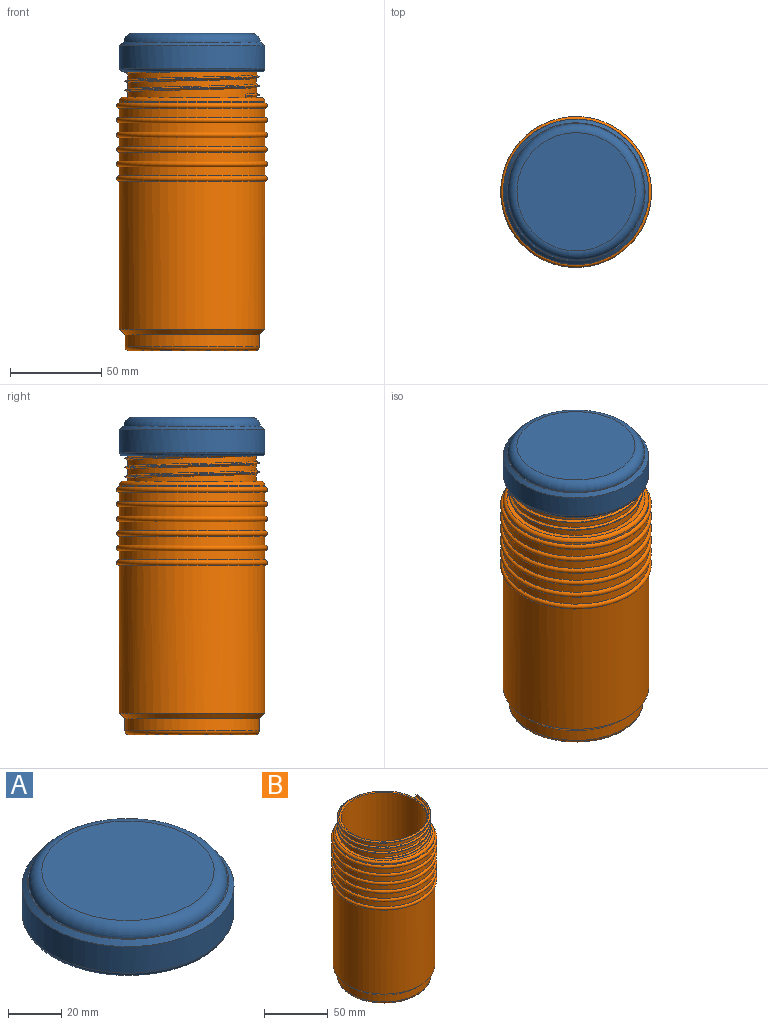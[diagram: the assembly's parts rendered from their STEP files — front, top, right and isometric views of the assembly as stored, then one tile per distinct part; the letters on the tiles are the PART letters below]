
ASSEMBLY  parts=2 mates=1
PART A: 16 faces, bbox 87.1x87.4x22.4 mm
  f0: plane 75.7x75.7mm, normal (0,0,1), area 110.6mm2, adj f12,f15
  f1: cylinder r=37.45mm len=74.9mm, axis (0,0,-1), area 2082.9mm2, adj f2,f7,f8,f9,f10
  f2: plane 75.7x75.7mm, normal (0,0,-1), area 94.6mm2, adj f1,f11
  f3: cylinder r=39.85mm len=79.7mm, axis (0,0,-1), area 3054.7mm2, adj f11,f12
  f4: cylinder r=32mm len=64mm, axis (0,0,-1), area 140.7mm2, adj f6,f14
  f5: plane 74.78x74.03mm, normal (0,0,-1), area 934.9mm2, adj f6,f7,f9,f10
  f6: cone r=32mm half-angle=45deg, axis (0,0,-1), area 143.3mm2, adj f4,f5
  f7: cone r=36.95mm half-angle=45deg, axis (0,0,-1), area 107.1mm2, adj f1,f5,f9,f10
  f8: plane 1.86x1.18mm, normal (-0.73,0.68,0), area 1.5mm2, adj f1,f9,f10
  f9: bspline ~86.49x74.9mm, area 1380.3mm2, adj f1,f5,f7,f8,f10
  f10: bspline ~86.49x74.9mm, area 1293.7mm2, adj f1,f5,f7,f8,f9
  f11: torus R=37.85mm, axis (0,0,1), area 772.3mm2, adj f2,f3
  f12: cone r=39.85mm half-angle=45deg, axis (0,0,-1), area 690.4mm2, adj f0,f3
  f13: plane 64.78x64.78mm, normal (0,0,1), area 3295.6mm2, adj f15
  f14: plane 64x64mm, normal (0,0,-1), area 3217mm2, adj f4
  f15: torus R=32.39mm, axis (0,0,-1), area 1696.6mm2, adj f0,f13
PART B: 38 faces, bbox 89.5x89.5x157.4 mm
  f0: cylinder r=39.85mm len=79.7mm, axis (0,0,-1), area 250.4mm2, adj f1,f18
  f1: torus R=39.85mm, axis (0,0,-1), area 1208.2mm2, adj f0,f2
  f2: cylinder r=39.85mm len=79.7mm, axis (0,0,-1), area 1251.9mm2, adj f1,f3
  f3: torus R=39.85mm, axis (0,0,-1), area 1208.2mm2, adj f2,f4
  f4: cylinder r=39.85mm len=79.7mm, axis (0,0,-1), area 1251.9mm2, adj f3,f5
  f5: torus R=39.85mm, axis (0,0,-1), area 1208.2mm2, adj f4,f6
  f6: cylinder r=39.85mm len=79.7mm, axis (0,0,-1), area 1251.9mm2, adj f5,f7
  f7: torus R=39.85mm, axis (0,0,-1), area 1208.2mm2, adj f6,f8
  f8: cylinder r=39.85mm len=79.7mm, axis (0,0,-1), area 1251.9mm2, adj f7,f9
  f9: torus R=39.85mm, axis (0,0,-1), area 1208.2mm2, adj f8,f10
  f10: cylinder r=39.85mm len=79.7mm, axis (0,0,-1), area 1251.9mm2, adj f9,f11
  f11: torus R=39.85mm, axis (0,0,-1), area 1208.2mm2, adj f10,f12
  f12: cylinder r=39.85mm len=81mm, axis (0,0,-1), area 20281.2mm2, adj f11,f29
  f13: cone r=39.85mm half-angle=89.9deg, axis (0,0,1), area 19.2mm2, adj f29,f30
  f14: cylinder r=33.6mm len=67.66mm, axis (0,0,-1), area 14284.5mm2, adj f15,f32
  f15: cone r=35.35mm half-angle=88.5deg, axis (0,0,1), area 309mm2, adj f14,f16,f20,f21,f22,f27
  f16: cylinder r=35.35mm len=70.7mm, axis (0,0,-1), area 2257.1mm2, adj f15,f17,f19,f24,f25,f26
  f17: plane 75.7x75.7mm, normal (0,0,1), area 575mm2, adj f16,f18
  f18: torus R=37.85mm, axis (0,0,-1), area 772.3mm2, adj f0,f17
  f19: plane 1.86x1.42mm, normal (0,1,0), area 1.5mm2, adj f16,f20,f21,f22
  f20: bspline ~70.7x40.82mm, area 109.7mm2, adj f15,f19,f22,f27
  f21: bspline ~53.02x40.82mm, area 28.9mm2, adj f15,f19,f22
  f22: bspline ~37.91x34.26mm, area 19.3mm2, adj f15,f19,f20,f21
  f23: plane 1.86x1.42mm, normal (0,1,0), area 1.5mm2, adj f25,f26,f27,f28
  f24: plane 1.86x1.04mm, normal (-0.73,0.68,0), area 1.5mm2, adj f16,f25,f26,f28
  f25: bspline ~85.33x73.9mm, area 1144.6mm2, adj f16,f23,f24,f28
  f26: bspline ~85.33x73.9mm, area 1145.1mm2, adj f16,f23,f24,f27,f28
  f27: cylinder r=35.35mm len=70.7mm, axis (0,0,-1), area 218.3mm2, adj f15,f20,f23,f26
  f28: bspline ~73.93x73.93mm, area 326mm2, adj f23,f24,f25,f26
  f29: cone r=36.85mm half-angle=45deg, axis (0,0,1), area 1022.9mm2, adj f12,f13
  f30: cylinder r=36.77mm len=73.53mm, axis (0,0,1), area 1548.9mm2, adj f13,f37
  f31: plane 69.53x69.53mm, normal (0,0,-1), area 3797.4mm2, adj f37
  f32: plane 74.7x74.7mm, normal (0,0,-1), area 835.5mm2, adj f14,f34
  f33: plane 74.7x74.7mm, normal (0,0,1), area 135.4mm2, adj f34,f36
  f34: cylinder r=37.35mm len=74.7mm, axis (0,0,1), area 15018.7mm2, adj f32,f33
  f35: plane 73.53x73.53mm, normal (0,0,1), area 4246.9mm2, adj f36
  f36: cylinder r=36.77mm len=73.53mm, axis (0,0,1), area 1386.1mm2, adj f33,f35
  f37: torus R=34.77mm, axis (0,0,1), area 711.4mm2, adj f30,f31
PLACE A rot(axis=(0,0,1),108.8deg) t=(-81.58,-11.58,3.01)mm
PLACE B rot(axis=(0,0,1),99.2deg) t=(-81.58,-11.58,18.25)mm fixed
MATE cylindrical B.f0 <-> A.f1  axis (0,0,-1) through (-81.58,-11.58,51.95)mm
